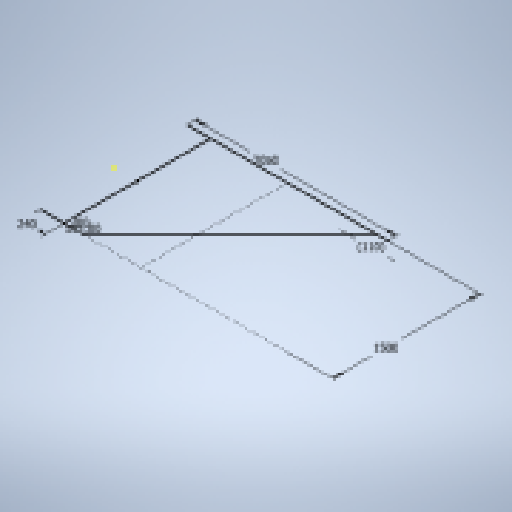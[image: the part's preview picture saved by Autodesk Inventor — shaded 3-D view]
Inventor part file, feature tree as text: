
AUTODESK INVENTOR PART (.ipt)
format: ipt  version: 2025 (Build 290162010, 162A)  size: 135,168 bytes
history: native  units: mm
features: sketch x1
ambient origin geometry x8: Origin, YZ Plane, XZ Plane, XY Plane, X Axis, Y Axis, Z Axis, Center Point
feature tree (1):
  sketch  "Sketch1"  dims[d5=2050.0mm d6=1500.0mm d10=240.0mm d11=200.0mm d12=110.0mm d13=135.0deg]
